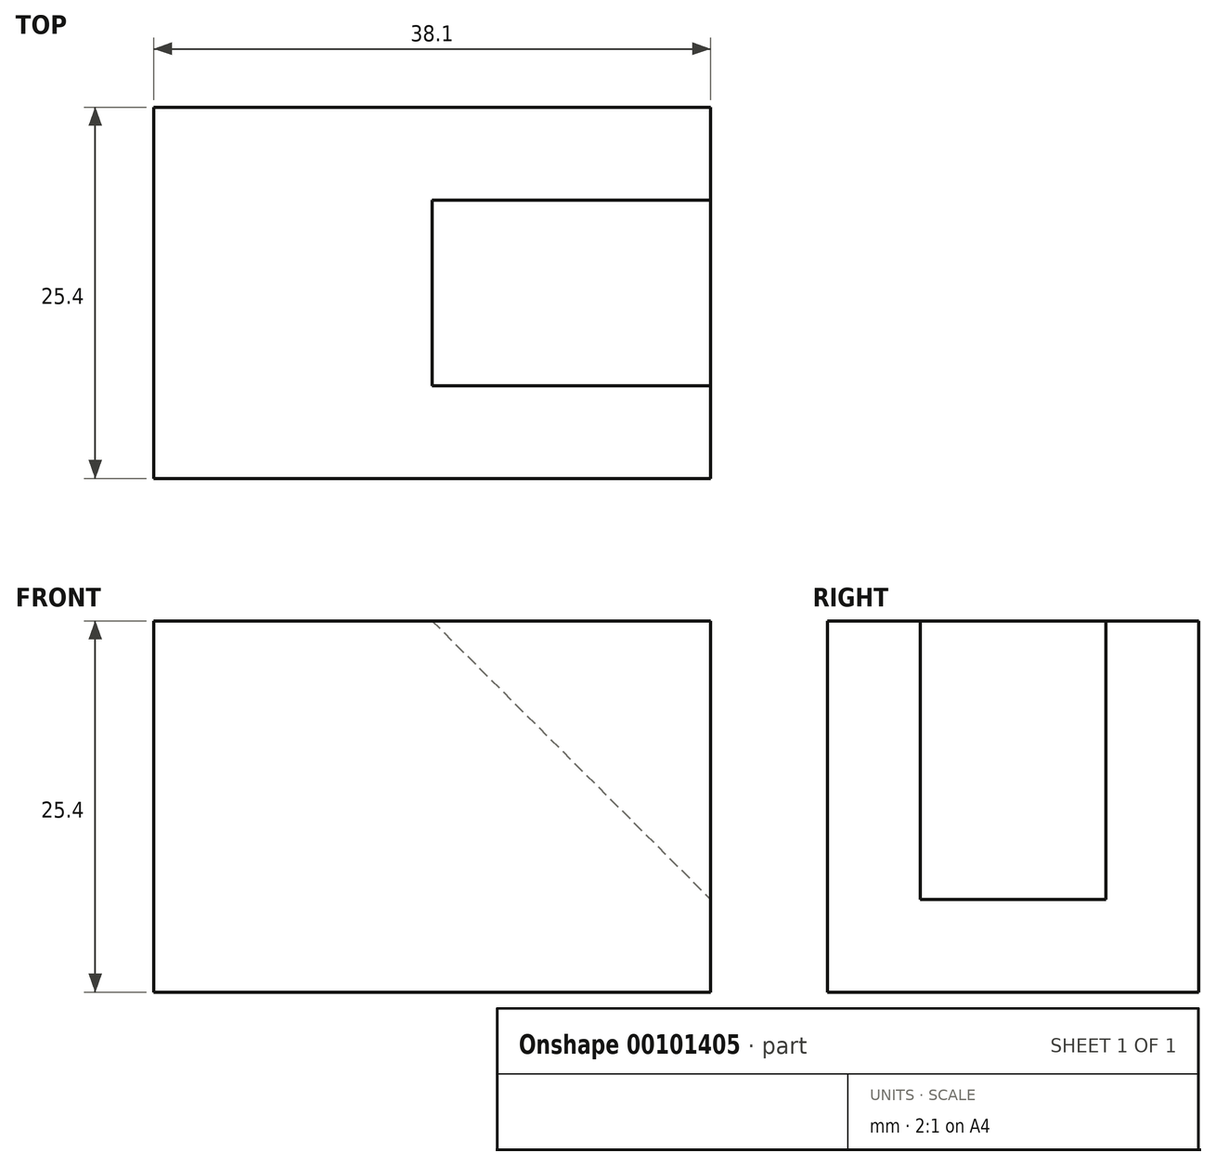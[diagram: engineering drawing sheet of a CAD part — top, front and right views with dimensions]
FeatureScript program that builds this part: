
annotation { "Feature Type Name" : "Feature", "Feature Type Description" : "" }
export const myFeature = defineFeature(function(context is Context, id is Id, definition is map)
    precondition{}
    {
        {
            var Q0;
            Q0=qCreatedBy(makeId("Front.planeOp"),FACE);
            var sketch = newSketch(context, id + "F0", { "sketchPlane" : qUnion([Q0])});
            skLineSegment(sketch, "E0.bottom", {"start": v(0, 0) * mm, "end": v(38.1, 0) * mm});
            skLineSegment(sketch, "E0.top", {"start": v(0, 25.4) * mm, "end": v(38.1, 25.4) * mm});
            skLineSegment(sketch, "E0.left", {"start": v(0, 0) * mm, "end": v(0, 25.4) * mm});
            skLineSegment(sketch, "E0.right", {"start": v(38.1, 0) * mm, "end": v(38.1, 25.4) * mm});
            skSolve(sketch);
        }
        {
            var Q0;
            Q0=makeQuery(id+"F0.imprint","IMPRINT",FACE,{"disambiguationData":[TD([[makeQuery(id+"F0.imprint","IMPRINT",EDGE,{"derivedFrom":sQuery(id+"F0.wireOp",EDGE,"E0.bottom")}),1.0]])]});
            extrude(context, id + "F1", {"entities" : qUnion([Q0]), "endBound" : BoundingType.SYMMETRIC, "depth" : 25.4 * mm});
        }
        {
            var Q0;
            Q0=qCreatedBy(makeId("Front.planeOp"),FACE);
            var sketch = newSketch(context, id + "F2", { "sketchPlane" : qUnion([Q0])});
            skLineSegment(sketch, "E1", {"start": v(19.05, 25.4) * mm, "end": v(38.1, 6.35) * mm});
            skLineSegment(sketch, "E2", {"start": v(19.05, 25.4) * mm, "end": v(38.1, 25.4) * mm});
            skLineSegment(sketch, "E3", {"start": v(38.1, 25.4) * mm, "end": v(38.1, 6.35) * mm});
            skSolve(sketch);
        }
        {
            var Q0;
            Q0 = qSketchRegion(id + "F2", true);
            extrude(context, id + "F3", {"entities" : qUnion([Q0]), "operationType" : NewBodyOperationType.REMOVE, "endBound" : BoundingType.SYMMETRIC, "oppositeDirection" : true, "depth" : 12.7 * mm});
        }
    });
